# Revit family: Fireplace-Gas-Regency-City_Series_New_York_View-CV40E
name_source: partatom
category: Mechanical Equipment
units: mm (PartAtom-declared; Revit-internal decimal feet)

## family parameters
Classification Number = 23.40.20.34.14
Cut with Voids When Loaded = Yes
Host = Face
Maintain Annotation Orientation = No
Part Type = Normal
Room Calculation Point = No
Round Connector Dimension = Use Diameter
Shared = No

## types (8) — shared parameters
Apparent Load = 120 VA
Assembly Code = D3020
Finish = Metal - Regency - Steel - Paint, Black Metallic
Frequency = 0 Hz
Installation and Service URL = https://www.regency-fire.com
Keynote = 10300
Manufacturer = Regency Fireplace Products
Manufacturer Fax Number = 604-946-4349
Material = Painted Stainless Steel
Number of Poles = 1
Opening Height = 1' - 3 1/16"
Performance URL = https://www.regency-fire.com
Phase = 1
Product Documentation Link = https://assets.regency-fire.com
Product Name = Regency® City Series™ New York View Gas Fireplace
Product Page URL = https://www.regency-fire.com
Product Size = Medium
Room Size = Medium
URL = https://www.regency-fire.com
Version = 2017 - v1.0a
Video Link = https://www.youtube.com
Voltage = 120 V
Warranty URL = https://www.regency-fire.com
zero-valued in all types: Power Factor

## per-type parameters (varying)
- 72" Direct Vent - NG: C Connector Depth=1' - 1"; C Gas Connection Height=0' - 3 7/8"; C Gas Connection Inset=3' - 0 1/4"; C Gas Connection Width=0' - 5"; C Height From Floor=1' - 0"; C Natural Gas=Yes; C Propane=No; CV40E=No; CV72E=Yes; Constraints=722; Default Elevation=1' - 0"; Depth=1' - 8 3/8"; Description=72" City Series New York View; Efficiency=63.06%; EnerGuide Rating=51.81%; Exhaust Air Connection Diameter=5"; Gas Type=Natural Gas; Height=3' - 10"; Height From Floor=1' - 0"; Manifold Pressure Max=3.5” W.C; Manifold Pressure Min=1.6” W.C; Maximum BTU=46500.0 Btu/h; Minimum BTU=32000.0 Btu/h; Model=CV72E-NG11; Opening Width=6' - 0 1/8"; Supply Air Connection Diameter=8"; Vent Connector Description=5” Inner / 8” Outer; Width=6' - 5 3/8"
- 40" Direct Vent - NG: C Connector Depth=0' - 11 7/16"; C Gas Connection Height=0' - 4"; C Gas Connection Inset=1' - 1"; C Gas Connection Width=0' - 3 1/2"; C Height From Floor=1' - 0"; C Natural Gas=Yes; C Propane=No; CV40E=Yes; CV72E=No; Constraints=402; Default Elevation=1' - 0"; Depth=1' - 6 11/16"; Description=40" City Series New York View; Efficiency=60.02%; EnerGuide Rating=55.59%; Exhaust Air Connection Diameter=4"; Gas Type=Natural Gas; Height=3' - 1 3/8"; Height From Floor=1' - 0"; Manifold Pressure Max=3.8” W.C.; Manifold Pressure Min=1.1” W.C.; Maximum BTU=28500.0 Btu/h; Minimum BTU=15500.0 Btu/h; Model=CV40E-NG11; Opening Width=3' - 4"; Supply Air Connection Diameter=7"; Vent Connector Description=4” Inner / 6-5/8” Outer; Width=3' - 10 1/4"
- 40" Power Vent - NG: C Connector Depth=0' - 11 7/16"; C Gas Connection Height=0' - 4"; C Gas Connection Inset=1' - 1"; C Gas Connection Width=0' - 3 1/2"; C Height From Floor=1' - 0"; C Natural Gas=Yes; C Propane=No; CV40E=Yes; CV72E=No; Constraints=404; Default Elevation=1' - 0"; Depth=1' - 6 11/16"; Description=40" City Series New York View; Efficiency=60.02%; EnerGuide Rating=55.59%; Exhaust Air Connection Diameter=4"; Gas Type=Natural Gas; Height=3' - 1 3/8"; Height From Floor=1' - 0"; Manifold Pressure Max=3.8” W.C.; Manifold Pressure Min=1.1” W.C.; Maximum BTU=28500.0 Btu/h; Minimum BTU=15500.0 Btu/h; Model=CV40EPV-NG11; Opening Width=3' - 4"; Supply Air Connection Diameter=7"; Vent Connector Description=4” Inner / 6-5/8” Outer; Width=3' - 10 1/4"
- 40" Direct Vent - LP: C Connector Depth=0' - 11 7/16"; C Gas Connection Height=0' - 4"; C Gas Connection Inset=1' - 1"; C Gas Connection Width=0' - 3 1/2"; C Height From Floor=1' - 0"; C Natural Gas=No; C Propane=Yes; CV40E=Yes; CV72E=No; Constraints=401; Default Elevation=1' - 0"; Depth=1' - 6 11/16"; Description=40" City Series New York View; Efficiency=60.68%; EnerGuide Rating=53.12%; Exhaust Air Connection Diameter=4"; Gas Type=Propane; Height=3' - 1 3/8"; Height From Floor=1' - 0"; Manifold Pressure Max=10.5” W.C.; Manifold Pressure Min=2.9” W.C.; Maximum BTU=28500.0 Btu/h; Minimum BTU=15500.0 Btu/h; Model=CV40E-LP11; Opening Width=3' - 4"; Supply Air Connection Diameter=7"; Vent Connector Description=4” Inner / 6-5/8” Outer; Width=3' - 10 1/4"
- 40" Power Vent - LP: C Connector Depth=0' - 11 7/16"; C Gas Connection Height=0' - 4"; C Gas Connection Inset=1' - 1"; C Gas Connection Width=0' - 3 1/2"; C Height From Floor=0' - 0"; C Natural Gas=No; C Propane=Yes; CV40E=Yes; CV72E=No; Constraints=403; Default Elevation=0' - 0"; Depth=1' - 6 11/16"; Description=40" City Series New York View; Efficiency=60.68%; EnerGuide Rating=53.12%; Exhaust Air Connection Diameter=4"; Gas Type=Propane; Height=3' - 1 3/8"; Height From Floor=0' - 0"; Manifold Pressure Max=10.5” W.C.; Manifold Pressure Min=2.9” W.C.; Maximum BTU=28500.0 Btu/h; Minimum BTU=15500.0 Btu/h; Model=CV40EPV-LP11; Opening Width=3' - 4"; Supply Air Connection Diameter=7"; Vent Connector Description=4” Inner / 6-5/8” Outer; Width=3' - 10 1/4"
- 72" Direct Vent - LP: C Connector Depth=1' - 1"; C Gas Connection Height=0' - 3 7/8"; C Gas Connection Inset=3' - 0 1/4"; C Gas Connection Width=0' - 5"; C Height From Floor=1' - 0"; C Natural Gas=No; C Propane=Yes; CV40E=No; CV72E=Yes; Constraints=721; Default Elevation=1' - 0"; Depth=1' - 8 3/8"; Description=72" City Series New York View; Efficiency=63.83%; EnerGuide Rating=60.61%; Exhaust Air Connection Diameter=5"; Gas Type=Propane; Height=3' - 10"; Height From Floor=1' - 0"; Manifold Pressure Max=10” W.C; Manifold Pressure Min=6.4” W.C; Maximum BTU=46500.0 Btu/h; Minimum BTU=36000.0 Btu/h; Model=CV72E-LP11; Opening Width=6' - 0 1/8"; Supply Air Connection Diameter=8"; Vent Connector Description=5” Inner / 8” Outer; Width=6' - 5 3/8"
- 72" Power Vent - LP: C Connector Depth=1' - 1"; C Gas Connection Height=0' - 3 7/8"; C Gas Connection Inset=3' - 0 1/4"; C Gas Connection Width=0' - 5"; C Height From Floor=1' - 0"; C Natural Gas=No; C Propane=Yes; CV40E=No; CV72E=Yes; Constraints=723; Default Elevation=1' - 0"; Depth=1' - 8 3/8"; Description=72" City Series New York View; Efficiency=63.83%; EnerGuide Rating=60.61%; Exhaust Air Connection Diameter=5"; Gas Type=Propane; Height=3' - 10"; Height From Floor=1' - 0"; Manifold Pressure Max=10” W.C; Manifold Pressure Min=6.4” W.C; Maximum BTU=46500.0 Btu/h; Minimum BTU=36000.0 Btu/h; Model=CV72EPV-LP11; Opening Width=6' - 0 1/8"; Supply Air Connection Diameter=8"; Vent Connector Description=5” Inner / 8” Outer; Width=6' - 5 3/8"
- 72" Power Vent - NG: C Connector Depth=1' - 1"; C Gas Connection Height=0' - 3 7/8"; C Gas Connection Inset=3' - 0 1/4"; C Gas Connection Width=0' - 5"; C Height From Floor=1' - 0"; C Natural Gas=Yes; C Propane=No; CV40E=No; CV72E=Yes; Constraints=724; Default Elevation=1' - 0"; Depth=1' - 8 3/8"; Description=72" City Series New York View; Efficiency=63.06%; EnerGuide Rating=51.81%; Exhaust Air Connection Diameter=5"; Gas Type=Natural Gas; Height=3' - 10"; Height From Floor=1' - 0"; Manifold Pressure Max=3.5” W.C; Manifold Pressure Min=1.6” W.C; Maximum BTU=46500.0 Btu/h; Minimum BTU=32000.0 Btu/h; Model=CV72EPV-NG11; Opening Width=6' - 0 1/8"; Supply Air Connection Diameter=8"; Vent Connector Description=5” Inner / 8” Outer; Width=6' - 5 3/8"

## geometry (parser evidence)
native form markers: Sweep x3
no freeform markers — native parametric forms only
